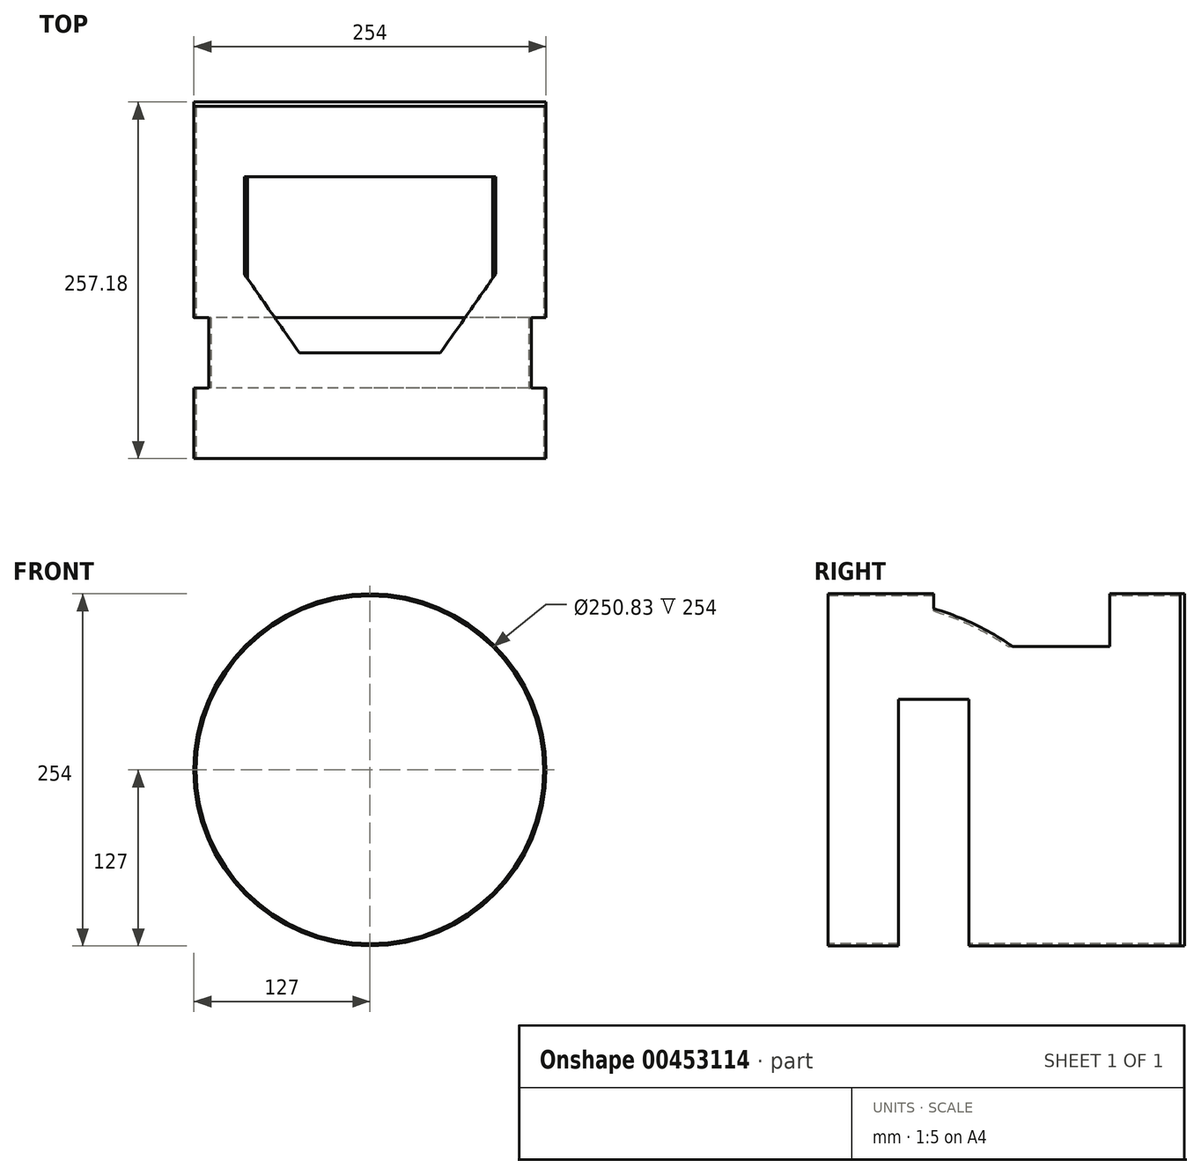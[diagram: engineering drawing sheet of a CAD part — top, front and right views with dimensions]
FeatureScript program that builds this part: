
annotation { "Feature Type Name" : "Feature", "Feature Type Description" : "" }
export const myFeature = defineFeature(function(context is Context, id is Id, definition is map)
    precondition{}
    {
        {
            var Q0;
            Q0=qCreatedBy(makeId("Front.planeOp"),FACE);
            var sketch = newSketch(context, id + "F0", { "sketchPlane" : qUnion([Q0])});
            skCircle(sketch, "E0", {"center": v(0, 0) * mm, "radius": 127 * mm});
            skCircle(sketch, "E1", {"center": v(0, 0) * mm, "radius": 125.41 * mm});
            skSolve(sketch);
        }
        {
            var Q0;
            Q0 = qSketchRegion(id + "F0", true);
            extrude(context, id + "F1", {"entities" : qUnion([Q0]), "oppositeDirection" : true, "depth" : 254 * mm});
        }
        {
            var Q0;
            Q0=qCreatedBy(makeId("Top.planeOp"),FACE);
            var sketch = newSketch(context, id + "F2", { "sketchPlane" : qUnion([Q0])});
            skLineSegment(sketch, "E2.bottom", {"start": v(139.7, 101.6) * mm, "end": v(-139.7, 101.6) * mm});
            skLineSegment(sketch, "E2.top", {"start": v(139.7, 50.8) * mm, "end": v(-139.7, 50.8) * mm});
            skLineSegment(sketch, "E2.left", {"start": v(139.7, 101.6) * mm, "end": v(139.7, 50.8) * mm});
            skLineSegment(sketch, "E2.right", {"start": v(-139.7, 101.6) * mm, "end": v(-139.7, 50.8) * mm});
            skPoint(sketch, "E2.middle", {"position": v(0, 76.2) * mm});
            skSolve(sketch);
        }
        {
            var Q0;
            Q0 = qSketchRegion(id + "F2", true);
            extrude(context, id + "F3", {"entities" : qUnion([Q0]), "operationType" : NewBodyOperationType.REMOVE, "oppositeDirection" : true, "depth" : 203.2 * mm, "hasSecondDirection" : true, "secondDirectionOppositeDirection" : false, "secondDirectionDepth" : 50.8 * mm});
        }
        {
            var Q0;
            Q0=qCreatedBy(makeId("Top.planeOp"),FACE);
            cPlane(context, id + "F4", {"entities" : qUnion([Q0]), "cplaneType" : CPlaneType.OFFSET, "offset" : 88.9 * mm, "width" : 152.4 * mm, "height" : 152.4 * mm});
        }
        {
            var Q0;
            Q0=qCreatedBy(id+"F4.planeOp",FACE);
            var sketch = newSketch(context, id + "F5", { "sketchPlane" : qUnion([Q0])});
            skLineSegment(sketch, "E3", {"start": v(0, 76.2) * mm, "end": v(-50.8, 76.2) * mm});
            skLineSegment(sketch, "E4", {"start": v(-50.8, 76.2) * mm, "end": v(-139.7, 203.2) * mm});
            skLineSegment(sketch, "E5", {"start": v(-139.7, 203.2) * mm, "end": v(0, 203.2) * mm});
            skLineSegment(sketch, "E6", {"start": v(0, 0) * mm, "end": v(0, 240.36) * mm, "construction": true});
            skLineSegment(sketch, "E7.MirrorCS", {"start": v(139.7, 203.2) * mm, "end": v(0, 203.2) * mm});
            skLineSegment(sketch, "E8.MirrorCS", {"start": v(50.8, 76.2) * mm, "end": v(139.7, 203.2) * mm});
            skLineSegment(sketch, "E9.MirrorCS", {"start": v(0, 76.2) * mm, "end": v(50.8, 76.2) * mm});
            skSolve(sketch);
        }
        {
            var Q0;
            Q0 = qSketchRegion(id + "F5", true);
            extrude(context, id + "F6", {"entities" : qUnion([Q0]), "operationType" : NewBodyOperationType.REMOVE, "depth" : 76.2 * mm});
        }
        {
            var Q0;
            Q0=makeQuery(id+"F1.opExtrude","CAP_FACE",FACE,{"disambiguationData":[OSD([sQuery(id+"F0.wireOp",EDGE,"E0"),sQuery(id+"F0.wireOp",EDGE,"E1")])],"isStart":false});
            var sketch = newSketch(context, id + "F7", { "sketchPlane" : qUnion([Q0])});
            skCircle(sketch, "E10", {"center": v(0, 0) * mm, "radius": 126.98 * mm});
            skSolve(sketch);
        }
        {
            var Q0;
            Q0 = qSketchRegion(id + "F7", true);
            extrude(context, id + "F8", {"entities" : qUnion([Q0]), "operationType" : NewBodyOperationType.ADD, "depth" : 3.17 * mm});
        }
    });
